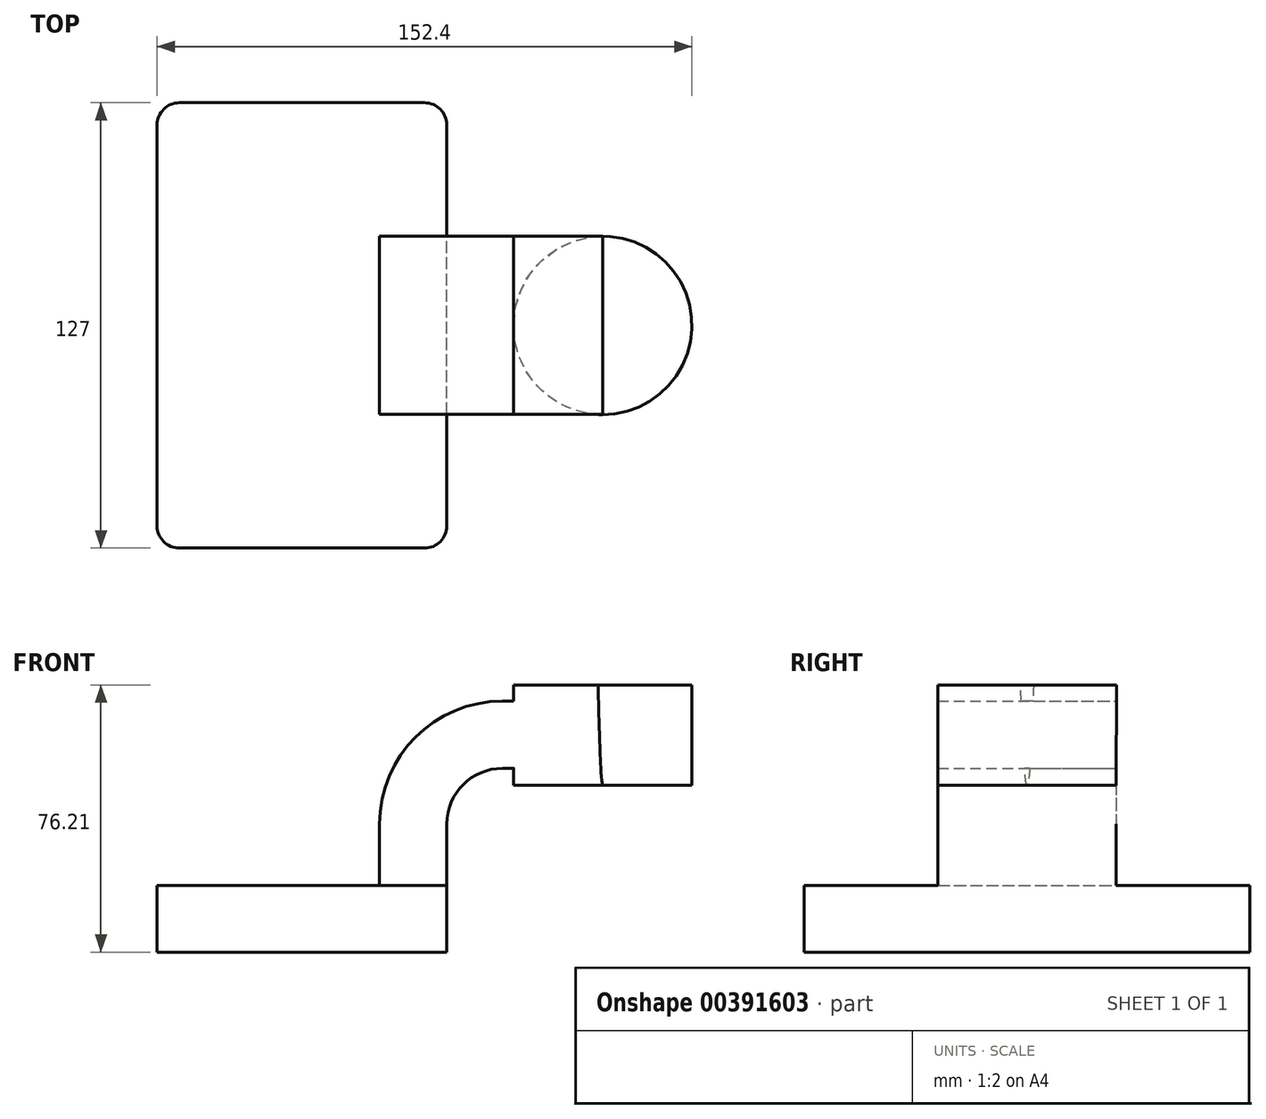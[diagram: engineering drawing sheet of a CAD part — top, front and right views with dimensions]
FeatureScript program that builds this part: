
annotation { "Feature Type Name" : "Feature", "Feature Type Description" : "" }
export const myFeature = defineFeature(function(context is Context, id is Id, definition is map)
    precondition{}
    {
        {
            var Q0;
            Q0=qCreatedBy(makeId("Front.planeOp"),FACE);
            var sketch = newSketch(context, id + "F0", { "sketchPlane" : qUnion([Q0])});
            skLineSegment(sketch, "E0.bottom", {"start": v(41.28, -9.52) * mm, "end": v(-41.28, -9.52) * mm});
            skLineSegment(sketch, "E0.top", {"start": v(41.28, 9.53) * mm, "end": v(-41.28, 9.53) * mm});
            skLineSegment(sketch, "E0.left", {"start": v(41.28, -9.52) * mm, "end": v(41.28, 9.53) * mm});
            skLineSegment(sketch, "E0.right", {"start": v(-41.28, -9.52) * mm, "end": v(-41.28, 9.53) * mm});
            skPoint(sketch, "E0.middle", {"position": v(0, 0) * mm});
            skLineSegment(sketch, "E1.bottom", {"start": v(111.12, 38.1) * mm, "end": v(60.32, 38.1) * mm});
            skLineSegment(sketch, "E1.top", {"start": v(111.12, 66.68) * mm, "end": v(60.32, 66.68) * mm});
            skLineSegment(sketch, "E1.left", {"start": v(111.12, 38.1) * mm, "end": v(111.12, 66.68) * mm});
            skLineSegment(sketch, "E1.right", {"start": v(60.32, 38.1) * mm, "end": v(60.32, 66.68) * mm});
            skPoint(sketch, "E1.middle", {"position": v(85.72, 52.39) * mm});
            skLineSegment(sketch, "E2", {"start": v(41.28, 9.53) * mm, "end": v(41.28, 27) * mm});
            skArc(sketch, "E3", {"start": v(41.27, 27) * mm, "mid": v(45.92, 38.23) * mm, "end": v(57.15, 42.88) * mm});
            skLineSegment(sketch, "E4", {"start": v(57.15, 42.88) * mm, "end": v(85.7, 42.88) * mm});
            skLineSegment(sketch, "E5.0", {"start": v(57.15, 62.05) * mm, "end": v(85.7, 62.05) * mm});
            skArc(sketch, "E5.1", {"start": v(22.1, 27) * mm, "mid": v(32.36, 51.79) * mm, "end": v(57.15, 62.05) * mm});
            skLineSegment(sketch, "E5.2", {"start": v(22.1, 9.53) * mm, "end": v(22.1, 27) * mm});
            skLineSegment(sketch, "E6", {"start": v(85.72, 38.1) * mm, "end": v(85.7, 66.68) * mm});
            skPoint(sketch, "E6.endSnap0", {"position": v(85.72, 66.68) * mm});
            skFitSpline(sketch, "E7", {"points": [v(-41.28, 9.52) * mm, v(57.15, 62.05) * mm], "startDerivative": vector(6.48, 60.45) * mm, "endDerivative": vector(146.74, -7.73) * mm});
            skSolve(sketch);
        }
        {
            var Q0;
            Q0=makeQuery(id+"F0.imprint","IMPRINT",FACE,{"disambiguationData":[TD([[makeQuery(id+"F0.imprint","IMPRINT",EDGE,{"derivedFrom":sQuery(id+"F0.wireOp",EDGE,"E0.bottom")}),-1.0]])]});
            extrude(context, id + "F1", {"entities" : qUnion([Q0]), "endBound" : BoundingType.SYMMETRIC, "depth" : 127 * mm});
        }
        {
            var Q0;
            {var subQ1=sQuery(id+"F0.wireOp",EDGE,"E2");Q0=makeQuery(id+"F0.imprint","IMPRINT",FACE,{"disambiguationData":[TD([[makeQuery(id+"F0.imprint","IMPRINT",EDGE,{"derivedFrom":subQ1}),1.0]])]});}
            var Q1;
            {var subQ6=sQuery(id+"F0.wireOp",EDGE,"E6");Q1=makeQuery(id+"F0.imprint","IMPRINT",FACE,{"disambiguationData":[TD([[makeQuery(id+"F0.imprint","IMPRINT",EDGE,{"derivedFrom":subQ6}),1.0]])]});}
            extrude(context, id + "F2", {"entities" : qUnion([Q0, Q1]), "operationType" : NewBodyOperationType.ADD, "endBound" : BoundingType.SYMMETRIC, "depth" : 50.8 * mm});
        }
        {
            var Q0;
            Q0=makeQuery(id+"F0.imprint","IMPRINT",FACE,{"disambiguationData":[TD([[makeQuery(id+"F0.imprint","IMPRINT",EDGE,{"derivedFrom":sQuery(id+"F0.wireOp",EDGE,"E5.1")}),1.0]])]});
            extrude(context, id + "F3", {"entities" : qUnion([Q0]), "operationType" : NewBodyOperationType.ADD, "depth" : 15.88 * mm});
        }
        {
            var Q0;
            {var subQ0=sQuery(id+"F0.wireOp",EDGE,"E1.left");Q0=makeQuery(id+"F0.imprint","IMPRINT",FACE,{"disambiguationData":[TD([[makeQuery(id+"F0.imprint","IMPRINT",EDGE,{"derivedFrom":subQ0}),1.0]])]});}
            var Q1;
            Q1=sQuery(id+"F0.wireOp",EDGE,"E6");
            revolve(context, id + "F4", {"operationType" : NewBodyOperationType.ADD, "entities" : qUnion([Q0]), "axis" : qUnion([Q1]), "revolveType" : RevolveType.FULL});
        }
        {
            var Q0;
            Q0=makeQuery(id+"F1.opExtrude","CAP_EDGE",EDGE,{"disambiguationData":[OSD([sQuery(id+"F0.wireOp",EDGE,"E0.right")])],"isStart":false});
            var Q1;
            Q1=makeQuery(id+"F1.opExtrude","CAP_EDGE",EDGE,{"disambiguationData":[OSD([sQuery(id+"F0.wireOp",EDGE,"E0.left")])],"isStart":false});
            var Q2;
            Q2=makeQuery(id+"F1.opExtrude","CAP_EDGE",EDGE,{"disambiguationData":[OSD([sQuery(id+"F0.wireOp",EDGE,"E0.left")])],"isStart":true});
            var Q3;
            Q3=makeQuery(id+"F1.opExtrude","CAP_EDGE",EDGE,{"disambiguationData":[OSD([sQuery(id+"F0.wireOp",EDGE,"E0.right")])],"isStart":true});
            fillet(context, id + "F5", {"entities" : qUnion([Q0, Q1, Q2, Q3]), "radius" : 6.35 * mm, "tangentPropagation" : true, "allowEdgeOverflow" : false});
        }
    });
